# Revit family: NBS_DudleyIndustriesLimited_TltPprBulkDpnsrs_Anti-ligatureJumboToiletRollDispenser
name_source: partatom
category: Furniture
revit_build: Autodesk Revit 2018 (Build: 20190510_1515(x64)
units: mm (PartAtom-declared; Revit-internal decimal feet)

## family parameters
Cut with Voids When Loaded = No
Host = Face
Room Calculation Point = No
Shared = No

## types (1)
- Anti-ligatureJumboToiletRollDispenser
    AssetType = Fixed
    BIMObjectName = NBS_DudleyIndustriesLimited_ToiletPaperBulkDispensers_Anti-ligatureJumboToiletRollDispenser
    Category = Pr_40_70_22_90:Toilet paper dispensers
    Color = White, Blue
    Default Elevation = 1050 mm
    Description = Anti-ligature jumbo toilet roll dispenser
    DispenserMaterial = NBS_DudleyIndustriesLimited_StainlessSteel_Brushed
    DurationUnit = year
    Features = Suitable for different paper types, easy to refill, recessed lock protects the contents
    Finish = Brushed stainless steel
    IfcExportAs = IfcFurnitureType
    IfcExportType = UNDEFINED
    IsBuiltIn = Yes
    ManufacturerName = Dudley Industries Limited
    ManufacturerURL = www.dudleyindustries.com
    Material = Stainless steel
    MaterialsBody = Stainless steel
    MaterialsFinishAndColour = White, blue, brushed stainless steel
    ModelNumber = 89420, 89422
    ModelReference = Anti-ligatureJumboToiletRollDispenser
    NBSCertification = www.nationalbimlibrary.com/cert/ylmnfnja
    NBSDescription = Toilet paper bulk dispensers
    NBSReference = 45-35-72/366
    Name = ToiletPaperBulkDispensers_Anti-ligatureJumboToiletRollDispenser_DudleyIndustriesLimited
    NominalDepth = 140 mm  [stored 0.459318 ft]
    NominalHeight = 398 mm  [stored 1.30577 ft]
    NominalLength = 0 mm  [stored 0 ft]
    NominalWidth = 400 mm  [stored 1.31234 ft]
    Packing = 1 piece
    ProductInformation = https://www.dudleyindustries.com
    Shape = Rectangular
    Size = 140 x 398 x 400 mm
    Status = UNSET
    Style = Roll dispenser
    Uniclass2015Code = Pr_40_70_22_90
    Uniclass2015Title = Toilet paper dispensers
    Uniclass2015Version = Products v1.18
    Version = 1
    WallPlateMaterial = NBS_DudleyIndustriesLimited_StainlessSteel_Brushed
    WarrantyDescription = 10 Years
    WarrantyDurationUnit = year

note: [stored X ft] marks values corroborated as IEEE doubles in the binary element streams (Revit-internal decimal feet)

## geometry (parser evidence)
native form markers: Sweep x2
no freeform markers — native parametric forms only
